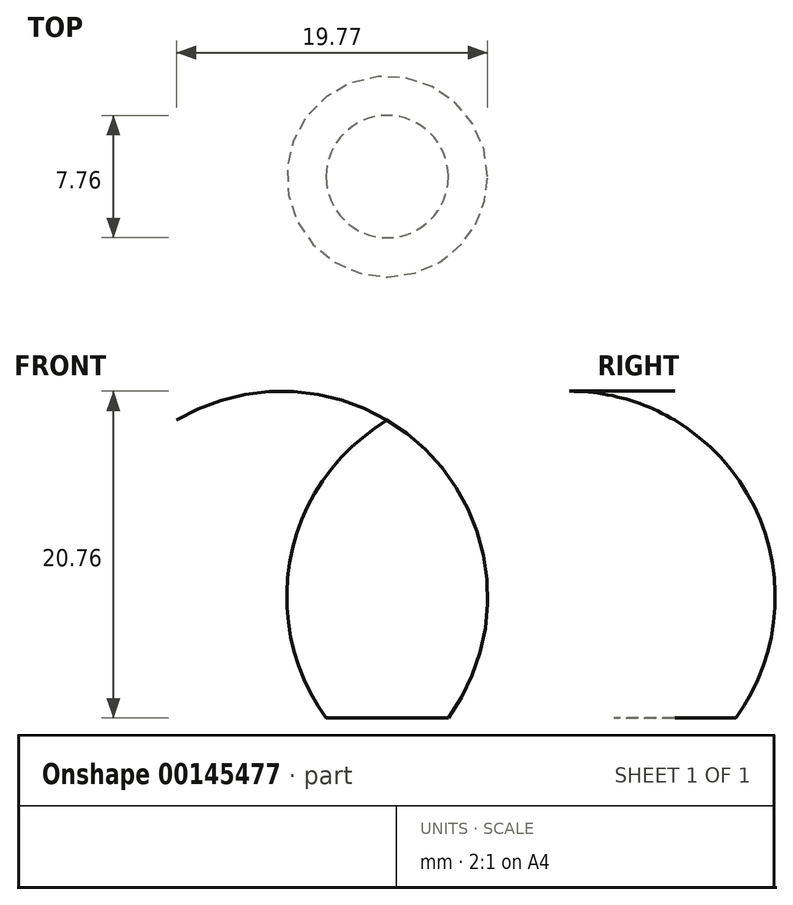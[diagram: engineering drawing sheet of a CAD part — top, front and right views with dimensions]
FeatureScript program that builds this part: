
annotation { "Feature Type Name" : "Feature", "Feature Type Description" : "" }
export const myFeature = defineFeature(function(context is Context, id is Id, definition is map)
    precondition{}
    {
        {
            var Q0;
            Q0=qCreatedBy(makeId("Front.planeOp"),FACE);
            var sketch = newSketch(context, id + "F0", { "sketchPlane" : qUnion([Q0])});
            skLineSegment(sketch, "E0", {"start": v(-35.41, -9.94) * mm, "end": v(-31.53, -9.94) * mm});
            skLineSegment(sketch, "E1", {"start": v(-31.53, -9.94) * mm, "end": v(-31.53, 8.97) * mm});
            skArc(sketch, "E2", {"start": v(-31.53, 8.97) * mm, "mid": v(-37.64, 0.37) * mm, "end": v(-35.41, -9.94) * mm});
            skSolve(sketch);
        }
        {
            var Q0;
            Q0=makeQuery(id+"F0.imprint","IMPRINT",FACE,{"disambiguationData":[TD([[makeQuery(id+"F0.imprint","IMPRINT",EDGE,{"derivedFrom":sQuery(id+"F0.wireOp",EDGE,"E0")}),1.0]])]});
            var Q1;
            Q1=sQuery(id+"F0.wireOp",EDGE,"E1");
            revolve(context, id + "F1", {"entities" : qUnion([Q0]), "axis" : qUnion([Q1]), "revolveType" : RevolveType.FULL});
        }
    });
